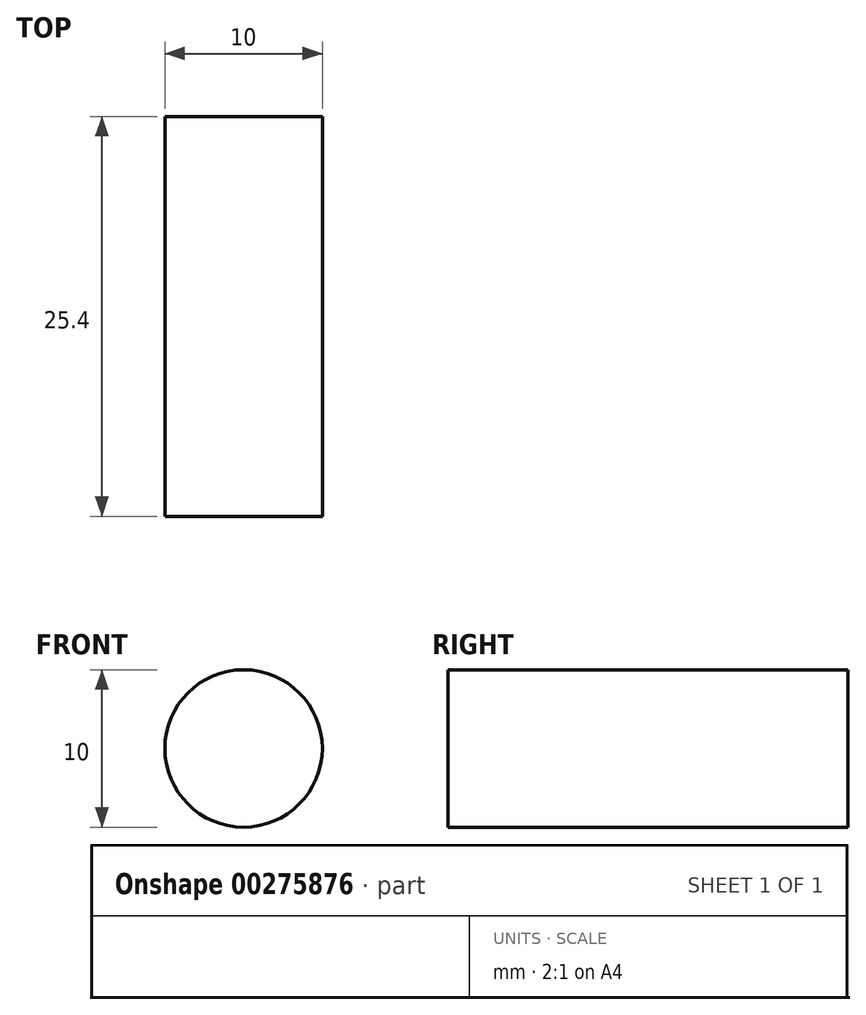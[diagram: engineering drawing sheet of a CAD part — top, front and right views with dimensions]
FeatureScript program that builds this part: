
annotation { "Feature Type Name" : "Feature", "Feature Type Description" : "" }
export const myFeature = defineFeature(function(context is Context, id is Id, definition is map)
    precondition{}
    {
        {
            var Q0;
            Q0=qCreatedBy(makeId("Front.planeOp"),FACE);
            var sketch = newSketch(context, id + "F0", { "sketchPlane" : qUnion([Q0])});
            skCircle(sketch, "E0", {"center": v(0, 0) * mm, "radius": 5 * mm});
            skSolve(sketch);
        }
        {
            var Q0;
            Q0=makeQuery(id+"F0.imprint","IMPRINT",FACE,{"disambiguationData":[TD([[makeQuery(id+"F0.imprint","IMPRINT",EDGE,{"derivedFrom":sQuery(id+"F0.wireOp",EDGE,"E0")}),1.0]])]});
            extrude(context, id + "F1", {"entities" : qUnion([Q0]), "depth" : 25.4 * mm});
        }
    });
